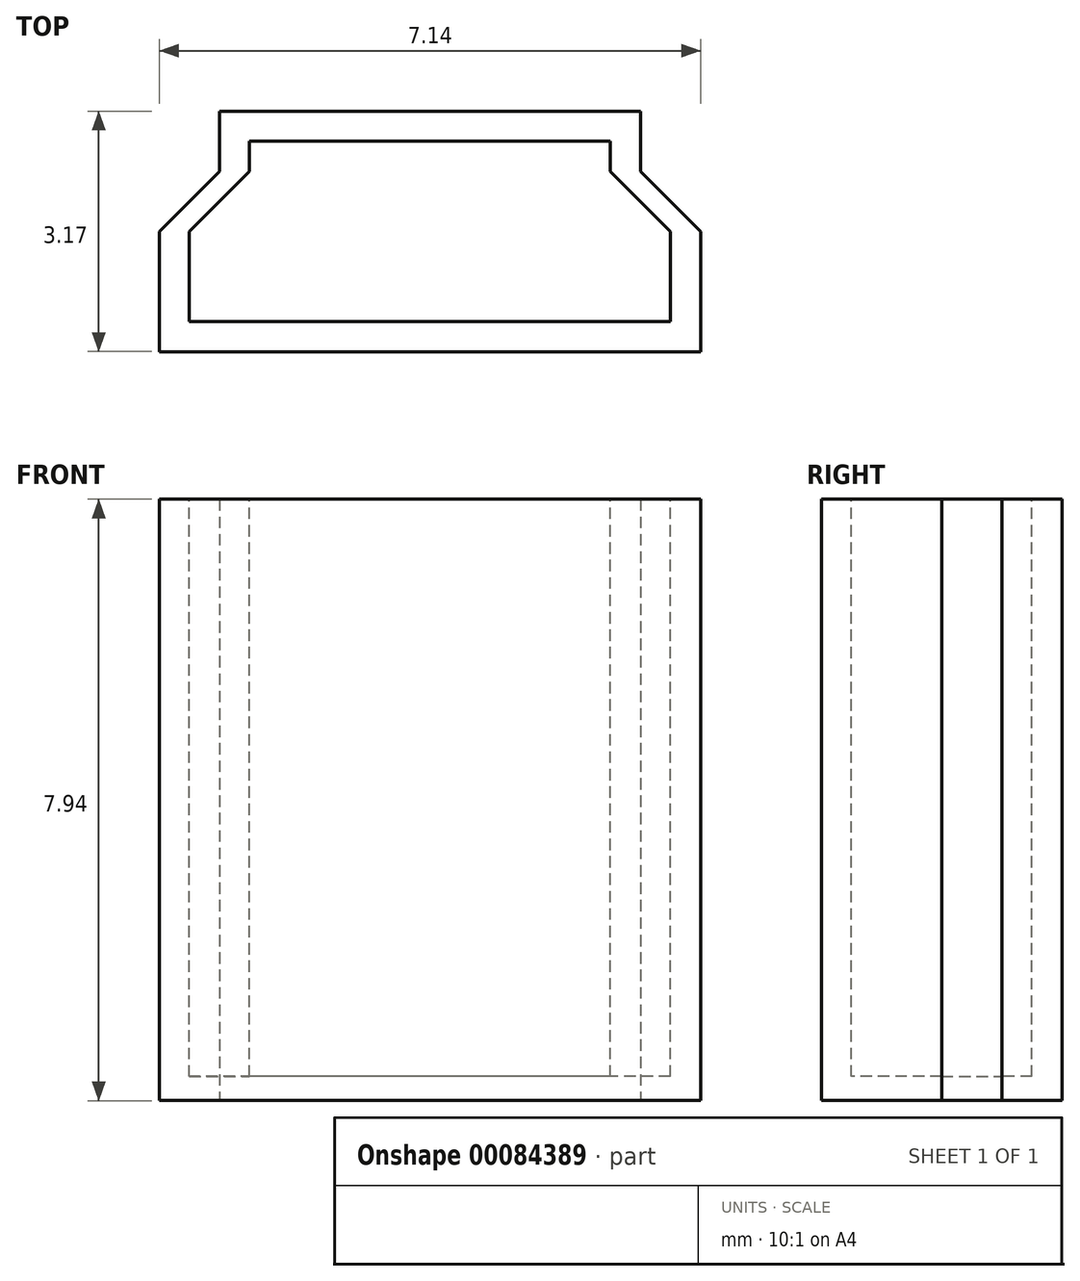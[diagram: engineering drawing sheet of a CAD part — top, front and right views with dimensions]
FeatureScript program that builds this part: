
annotation { "Feature Type Name" : "Feature", "Feature Type Description" : "" }
export const myFeature = defineFeature(function(context is Context, id is Id, definition is map)
    precondition{}
    {
        {
            var Q0;
            Q0=qCreatedBy(makeId("Front.planeOp"),FACE);
            var sketch = newSketch(context, id + "F0", { "sketchPlane" : qUnion([Q0])});
            skLineSegment(sketch, "E0", {"start": v(-21.96, -2.02) * mm, "end": v(-21.96, -9.96) * mm});
            skLineSegment(sketch, "E1", {"start": v(-21.96, -2.02) * mm, "end": v(-14.82, -2.02) * mm});
            skLineSegment(sketch, "E2", {"start": v(-21.96, -9.96) * mm, "end": v(-14.82, -9.96) * mm});
            skLineSegment(sketch, "E3", {"start": v(-14.82, -2.02) * mm, "end": v(-14.82, -9.96) * mm});
            skSolve(sketch);
        }
        {
            var Q0;
            Q0 = qSketchRegion(id + "F0", true);
            extrude(context, id + "F1", {"entities" : qUnion([Q0]), "depth" : 3.17 * mm});
        }
        {
            var Q0;
            Q0=makeQuery(id+"F1.opExtrude","SWEPT_FACE",FACE,{"disambiguationData":[OSD([sQuery(id+"F0.wireOp",EDGE,"E2")])]});
            var sketch = newSketch(context, id + "F2", { "sketchPlane" : qUnion([Q0])});
            skLineSegment(sketch, "E4", {"start": v(-14.82, 1.59) * mm, "end": v(-15.61, 0.8) * mm});
            skLineSegment(sketch, "E5", {"start": v(-15.61, 0) * mm, "end": v(-15.61, 0.8) * mm});
            skLineSegment(sketch, "E6", {"start": v(-21.96, 1.59) * mm, "end": v(-21.17, 0.8) * mm});
            skLineSegment(sketch, "E7", {"start": v(-21.17, 0.8) * mm, "end": v(-21.17, 0) * mm});
            skSolve(sketch);
        }
        {
            var Q0;
            {var subQ0=sQuery(id+"F2.wireOp",EDGE,"E6");Q0=makeQuery(id+"F2.imprint","IMPRINT",FACE,{"disambiguationData":[TD([[makeQuery(id+"F2.imprint","IMPRINT",EDGE,{"derivedFrom":subQ0}),-1.0]])]});}
            var Q1;
            {var subQ0=sQuery(id+"F2.wireOp",EDGE,"E4");Q1=makeQuery(id+"F2.imprint","IMPRINT",FACE,{"disambiguationData":[TD([[makeQuery(id+"F2.imprint","IMPRINT",EDGE,{"derivedFrom":subQ0}),1.0]])]});}
            extrude(context, id + "F3", {"entities" : qUnion([Q0, Q1]), "operationType" : NewBodyOperationType.REMOVE, "endBound" : BoundingType.THROUGH_ALL, "oppositeDirection" : true, "depth" : 25.4 * mm});
        }
        {
            var Q0;
            Q0=makeQuery(id+"F1.opExtrude","SWEPT_FACE",FACE,{"disambiguationData":[OSD([sQuery(id+"F0.wireOp",EDGE,"E1")])]});
            var sketch = newSketch(context, id + "F4", { "sketchPlane" : qUnion([Q0])});
            skLineSegment(sketch, "E8", {"start": v(-15.22, -3.18) * mm, "end": v(-15.22, -1.59) * mm});
            skLineSegment(sketch, "E9", {"start": v(-15.22, -1.59) * mm, "end": v(-16.01, -0.8) * mm});
            skLineSegment(sketch, "E10", {"start": v(-20.77, 0) * mm, "end": v(-20.77, -0.8) * mm});
            skLineSegment(sketch, "E11", {"start": v(-21.57, -1.59) * mm, "end": v(-21.57, -3.18) * mm});
            skLineSegment(sketch, "E12", {"start": v(-21.57, -1.59) * mm, "end": v(-20.77, -0.8) * mm});
            skLineSegment(sketch, "E13", {"start": v(-16.01, -0.8) * mm, "end": v(-16.01, 0) * mm});
            skLineSegment(sketch, "E14", {"start": v(-15.22, -2.78) * mm, "end": v(-21.57, -2.78) * mm});
            skLineSegment(sketch, "E15", {"start": v(-16.01, -0.4) * mm, "end": v(-20.77, -0.4) * mm});
            skSolve(sketch);
        }
        {
            var Q0;
            Q0 = qSketchRegion(id + "F4", true);
            extrude(context, id + "F5", {"entities" : qUnion([Q0]), "operationType" : NewBodyOperationType.REMOVE, "oppositeDirection" : true, "depth" : 7.62 * mm});
        }
    });
